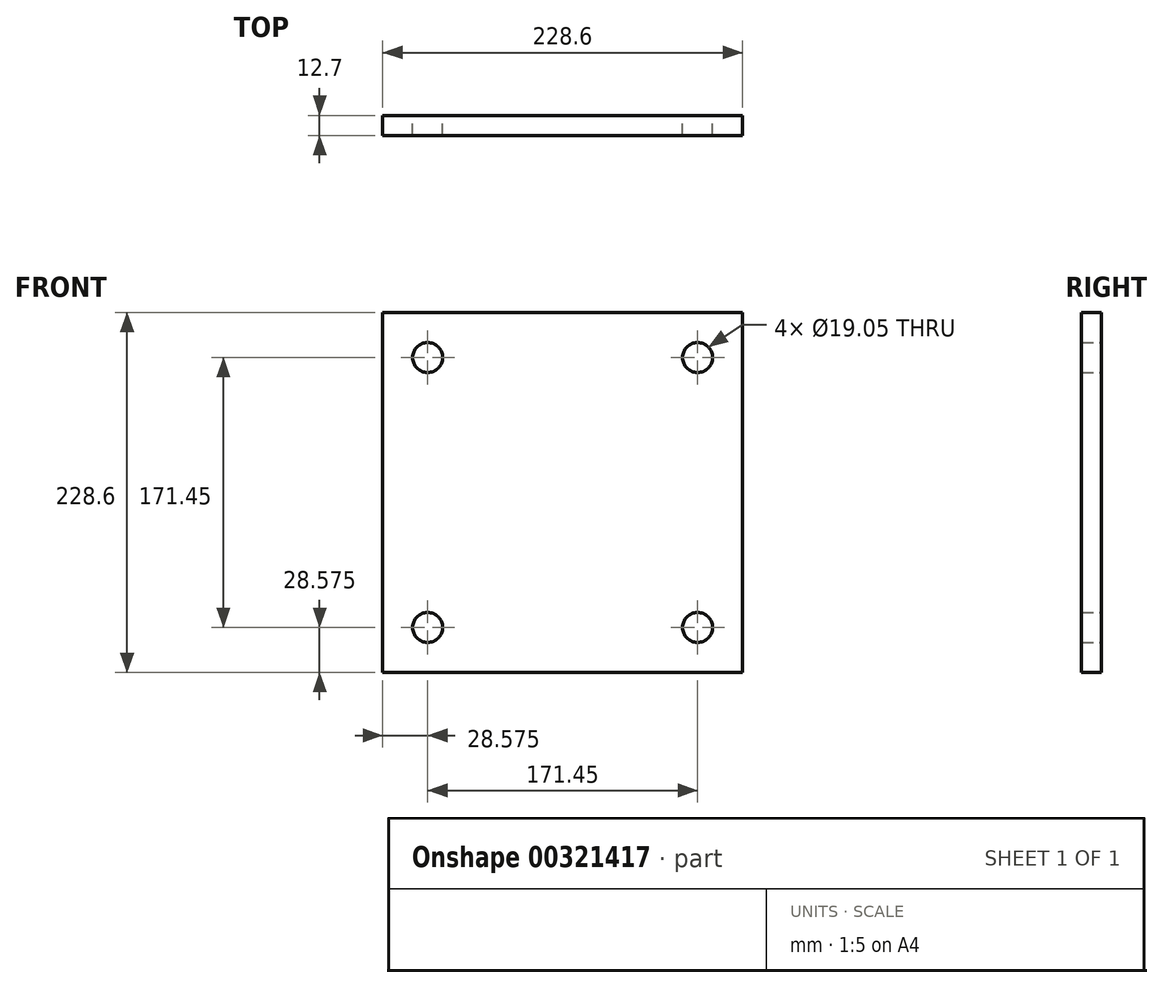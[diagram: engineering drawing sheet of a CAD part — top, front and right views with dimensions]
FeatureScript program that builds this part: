
annotation { "Feature Type Name" : "Feature", "Feature Type Description" : "" }
export const myFeature = defineFeature(function(context is Context, id is Id, definition is map)
    precondition{}
    {
        {
            var Q0;
            Q0=qCreatedBy(makeId("Front.planeOp"),FACE);
            var sketch = newSketch(context, id + "F0", { "sketchPlane" : qUnion([Q0])});
            skLineSegment(sketch, "E0.bottom", {"start": v(114.3, -114.3) * mm, "end": v(-114.3, -114.3) * mm});
            skLineSegment(sketch, "E0.top", {"start": v(114.3, 114.3) * mm, "end": v(-114.3, 114.3) * mm});
            skLineSegment(sketch, "E0.left", {"start": v(114.3, -114.3) * mm, "end": v(114.3, 114.3) * mm});
            skLineSegment(sketch, "E0.right", {"start": v(-114.3, -114.3) * mm, "end": v(-114.3, 114.3) * mm});
            skPoint(sketch, "E0.middle", {"position": v(0, 0) * mm});
            skCircle(sketch, "E1", {"center": v(-85.73, 85.73) * mm, "radius": 9.53 * mm});
            skCircle(sketch, "E2.1.0.0", {"center": v(85.72, 85.73) * mm, "radius": 9.53 * mm});
            skLineSegment(sketch, "E2.direction1", {"start": v(-85.73, 85.73) * mm, "end": v(85.72, 85.73) * mm, "construction": true});
            skCircle(sketch, "E3.1.0.0", {"center": v(-85.72, -85.72) * mm, "radius": 9.53 * mm});
            skCircle(sketch, "E3.2.0.0", {"center": v(-85.72, -257.18) * mm, "radius": 9.53 * mm});
            skLineSegment(sketch, "E3.direction1", {"start": v(-85.73, 85.73) * mm, "end": v(-85.72, -85.72) * mm, "construction": true});
            skCircle(sketch, "E4.1.0.0", {"center": v(85.72, -85.73) * mm, "radius": 9.53 * mm});
            skCircle(sketch, "E4.2.0.0", {"center": v(85.73, -257.18) * mm, "radius": 9.53 * mm});
            skLineSegment(sketch, "E4.direction1", {"start": v(85.72, 85.73) * mm, "end": v(85.72, -85.73) * mm, "construction": true});
            skSolve(sketch);
        }
        {
            var Q0;
            Q0=makeQuery(id+"F0.imprint","IMPRINT",FACE,{"disambiguationData":[TD([[makeQuery(id+"F0.imprint","IMPRINT",EDGE,{"derivedFrom":sQuery(id+"F0.wireOp",EDGE,"E0.bottom")}),-1.0]])]});
            extrude(context, id + "F1", {"entities" : qUnion([Q0]), "depth" : 12.7 * mm});
        }
    });
